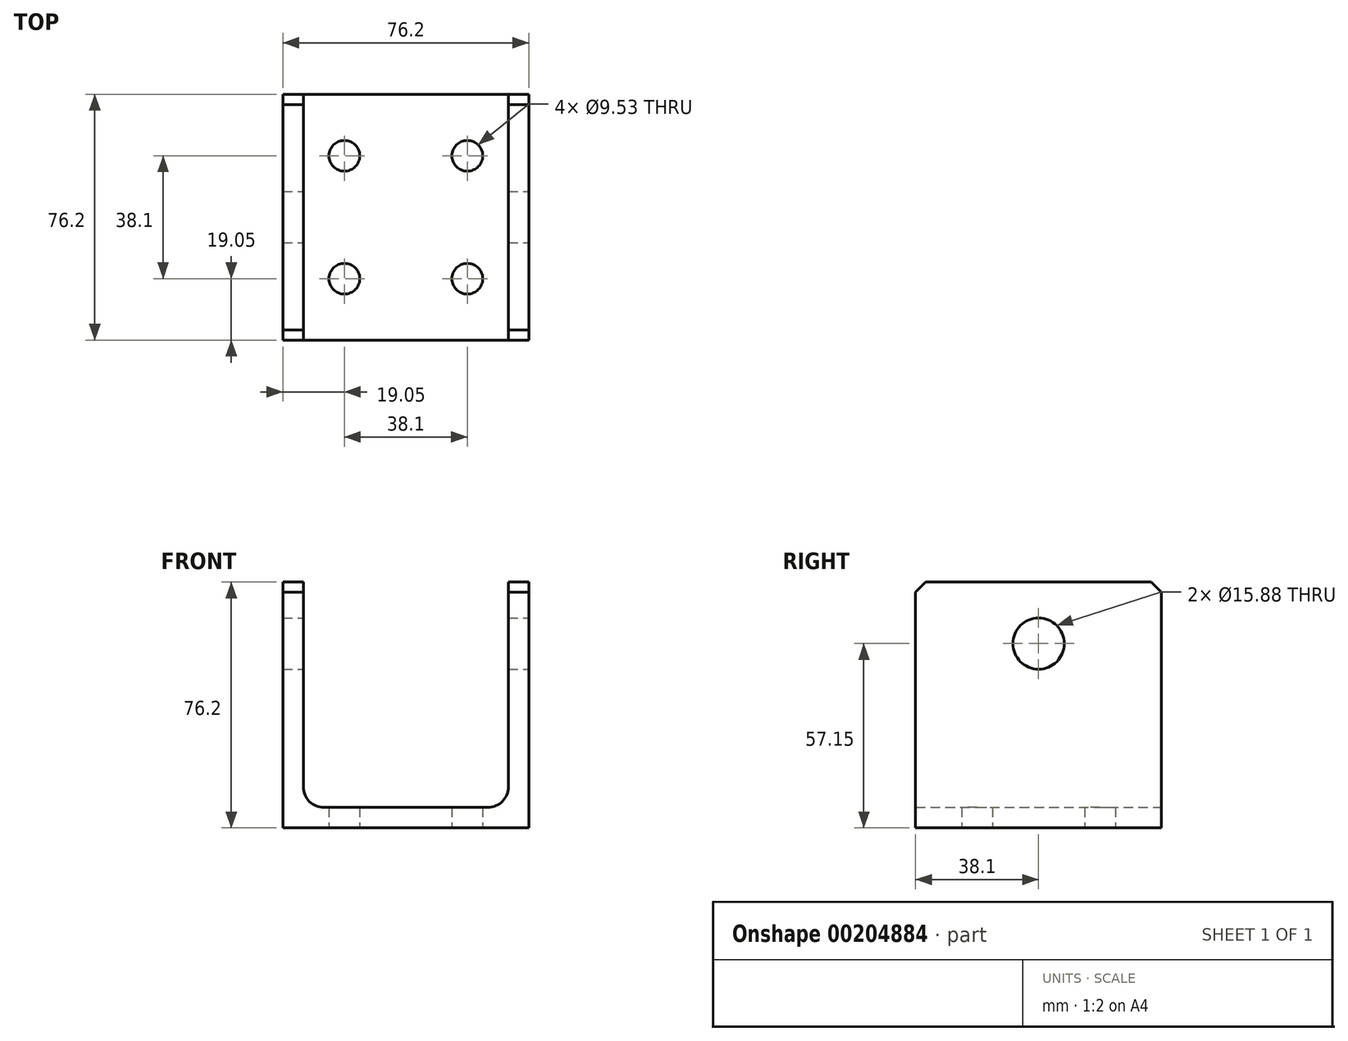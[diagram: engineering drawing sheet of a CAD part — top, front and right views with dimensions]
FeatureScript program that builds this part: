
annotation { "Feature Type Name" : "Feature", "Feature Type Description" : "" }
export const myFeature = defineFeature(function(context is Context, id is Id, definition is map)
    precondition{}
    {
        {
            var Q0;
            Q0=qCreatedBy(makeId("Front.planeOp"),FACE);
            var sketch = newSketch(context, id + "F0", { "sketchPlane" : qUnion([Q0])});
            skLineSegment(sketch, "E0.bottom", {"start": v(-38.1, 38.1) * mm, "end": v(-31.75, 38.1) * mm});
            skLineSegment(sketch, "E0.top", {"start": v(-38.1, -38.1) * mm, "end": v(38.1, -38.1) * mm});
            skLineSegment(sketch, "E0.left", {"start": v(-38.1, 38.1) * mm, "end": v(-38.1, -38.1) * mm});
            skLineSegment(sketch, "E0.right", {"start": v(38.1, 38.1) * mm, "end": v(38.1, -38.1) * mm});
            skPoint(sketch, "E0.middle", {"position": v(0, 0) * mm});
            skPoint(sketch, "E0.cornerSnap0", {"position": v(0, 38.1) * mm});
            skLineSegment(sketch, "E1.0", {"start": v(31.75, 38.1) * mm, "end": v(31.75, -25.4) * mm});
            skLineSegment(sketch, "E2.0", {"start": v(-25.4, -31.75) * mm, "end": v(25.4, -31.75) * mm});
            skLineSegment(sketch, "E3.0", {"start": v(-31.75, 38.1) * mm, "end": v(-31.75, -25.4) * mm});
            skLineSegment(sketch, "E4.trimOffspring", {"start": v(31.75, 38.1) * mm, "end": v(38.1, 38.1) * mm});
            skPoint(sketch, "E5.visualSharp", {"position": v(31.75, -31.75) * mm});
            skArc(sketch, "E5.filletArc", {"start": v(25.4, -31.75) * mm, "mid": v(29.9, -29.9) * mm, "end": v(31.75, -25.4) * mm});
            skPoint(sketch, "E6.visualSharp", {"position": v(-31.75, -31.75) * mm});
            skArc(sketch, "E6.filletArc", {"start": v(-31.75, -25.4) * mm, "mid": v(-29.9, -29.9) * mm, "end": v(-25.4, -31.75) * mm});
            skSolve(sketch);
        }
        {
            var Q0;
            Q0=makeQuery(id+"F0.imprint","IMPRINT",FACE,{"disambiguationData":[TD([[makeQuery(id+"F0.imprint","IMPRINT",EDGE,{"derivedFrom":sQuery(id+"F0.wireOp",EDGE,"E0.bottom")}),-1.0]])]});
            extrude(context, id + "F1", {"entities" : qUnion([Q0]), "depth" : 76.2 * mm});
        }
        {
            var Q0;
            Q0=makeQuery(id+"F1.opExtrude","SWEPT_FACE",FACE,{"disambiguationData":[OSD([sQuery(id+"F0.wireOp",EDGE,"E0.right")])]});
            var sketch = newSketch(context, id + "F2", { "sketchPlane" : qUnion([Q0])});
            skLineSegment(sketch, "E7", {"start": v(-38.1, 38.1) * mm, "end": v(-38.1, -38.1) * mm});
            skCircle(sketch, "E8", {"center": v(-38.1, 19.05) * mm, "radius": 7.94 * mm});
            skSolve(sketch);
        }
        {
            var Q0;
            Q0=sQuery(id+"F2.wireOp",VERTEX,"E8.center");
            var Q1;
            Q1=makeQuery(id+"F1.opExtrude","SWEPT_BODY",BODY,{"disambiguationData":[OSD([sQuery(id+"F0.wireOp",EDGE,"E0.bottom"),sQuery(id+"F0.wireOp",EDGE,"E0.top"),sQuery(id+"F0.wireOp",EDGE,"E0.left"),sQuery(id+"F0.wireOp",EDGE,"E0.right"),sQuery(id+"F0.wireOp",EDGE,"E1.0"),sQuery(id+"F0.wireOp",EDGE,"E2.0"),sQuery(id+"F0.wireOp",EDGE,"E3.0"),sQuery(id+"F0.wireOp",EDGE,"E4.trimOffspring"),sQuery(id+"F0.wireOp",EDGE,"E5.filletArc"),sQuery(id+"F0.wireOp",EDGE,"E6.filletArc")])]});
            hole(context, id + "F3", {"style" : HoleStyle.SIMPLE, "endStyle" : HoleEndStyle.THROUGH, "holeDiameter" : 15.88 * mm, "locations" : qUnion([Q0]), "scope" : qUnion([Q1]), "isTappedThrough" : true});
        }
        {
            var Q0;
            Q0=makeQuery(id+"F1.opExtrude","CAP_EDGE",EDGE,{"disambiguationData":[OSD([sQuery(id+"F0.wireOp",EDGE,"E0.bottom")])],"isStart":true});
            var Q1;
            Q1=makeQuery(id+"F1.opExtrude","CAP_EDGE",EDGE,{"disambiguationData":[OSD([sQuery(id+"F0.wireOp",EDGE,"E4.trimOffspring")])],"isStart":true});
            var Q2;
            Q2=makeQuery(id+"F1.opExtrude","CAP_EDGE",EDGE,{"disambiguationData":[OSD([sQuery(id+"F0.wireOp",EDGE,"E4.trimOffspring")])],"isStart":false});
            var Q3;
            Q3=makeQuery(id+"F1.opExtrude","CAP_EDGE",EDGE,{"disambiguationData":[OSD([sQuery(id+"F0.wireOp",EDGE,"E0.bottom")])],"isStart":false});
            chamfer(context, id + "F4", {"entities" : qUnion([Q0, Q1, Q2, Q3]), "width" : 3.17 * mm, "tangentPropagation" : true});
        }
        {
            var Q0;
            Q0=makeQuery(id+"F1.opExtrude","SWEPT_FACE",FACE,{"disambiguationData":[OSD([sQuery(id+"F0.wireOp",EDGE,"E0.top")])]});
            var sketch = newSketch(context, id + "F5", { "sketchPlane" : qUnion([Q0])});
            skCircle(sketch, "E9", {"center": v(-19.05, 57.15) * mm, "radius": 4.76 * mm});
            skCircle(sketch, "E10", {"center": v(19.05, 57.15) * mm, "radius": 4.76 * mm});
            skCircle(sketch, "E11", {"center": v(-19.05, 19.05) * mm, "radius": 4.76 * mm});
            skCircle(sketch, "E12", {"center": v(19.05, 19.05) * mm, "radius": 4.76 * mm});
            skSolve(sketch);
        }
        {
            var Q0;
            Q0=sQuery(id+"F5.wireOp",VERTEX,"E9.center");
            var Q1;
            Q1=sQuery(id+"F5.wireOp",VERTEX,"E10.center");
            var Q2;
            Q2=sQuery(id+"F5.wireOp",VERTEX,"E11.center");
            var Q3;
            Q3=sQuery(id+"F5.wireOp",VERTEX,"E12.center");
            var Q4;
            Q4=makeQuery(id+"F1.opExtrude","SWEPT_BODY",BODY,{"disambiguationData":[OSD([sQuery(id+"F0.wireOp",EDGE,"E0.bottom"),sQuery(id+"F0.wireOp",EDGE,"E0.top"),sQuery(id+"F0.wireOp",EDGE,"E0.left"),sQuery(id+"F0.wireOp",EDGE,"E0.right"),sQuery(id+"F0.wireOp",EDGE,"E1.0"),sQuery(id+"F0.wireOp",EDGE,"E2.0"),sQuery(id+"F0.wireOp",EDGE,"E3.0"),sQuery(id+"F0.wireOp",EDGE,"E4.trimOffspring"),sQuery(id+"F0.wireOp",EDGE,"E5.filletArc"),sQuery(id+"F0.wireOp",EDGE,"E6.filletArc")])]});
            hole(context, id + "F6", {"style" : HoleStyle.SIMPLE, "endStyle" : HoleEndStyle.THROUGH, "holeDiameter" : 9.52 * mm, "locations" : qUnion([Q0, Q1, Q2, Q3]), "scope" : qUnion([Q4]), "isTappedThrough" : true});
        }
    });
